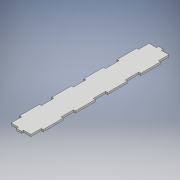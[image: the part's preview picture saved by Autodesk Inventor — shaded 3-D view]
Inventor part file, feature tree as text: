
AUTODESK INVENTOR PART (.ipt)
format: ipt  version: 2018 (Build 220112000, 112)  size: 178,176 bytes
history: native  units: mm
features: extrude x2, sketch x2, plane x1, mirror x1, projected_geometry x1
ambient origin geometry x8: Origin, YZ Plane, XZ Plane, XY Plane, X Axis, Y Axis, Z Axis, Center Point
bodies: Solid1 (feature_tree)
feature tree (7):
  extrude  "Extrusion1"  Depth=4.0mm
  extrude  "Extrusion2"  Depth=40.0mm
  plane  "Work Plane1"
  mirror  "Mirror1"
  sketch  "Sketch1"  dims[d1=40.0mm d2=4.0mm]
  sketch  "Sketch2"  dims[d3=40.0mm d4=40.0mm d5=40.0mm d6=40.0mm d7=279.2mm d8=4.0mm d9=0.0mm d10=10.0mm d11=4.0mm d12=4.0mm d13=0.0mm]
  projected_geometry  "Projected Loop1"
